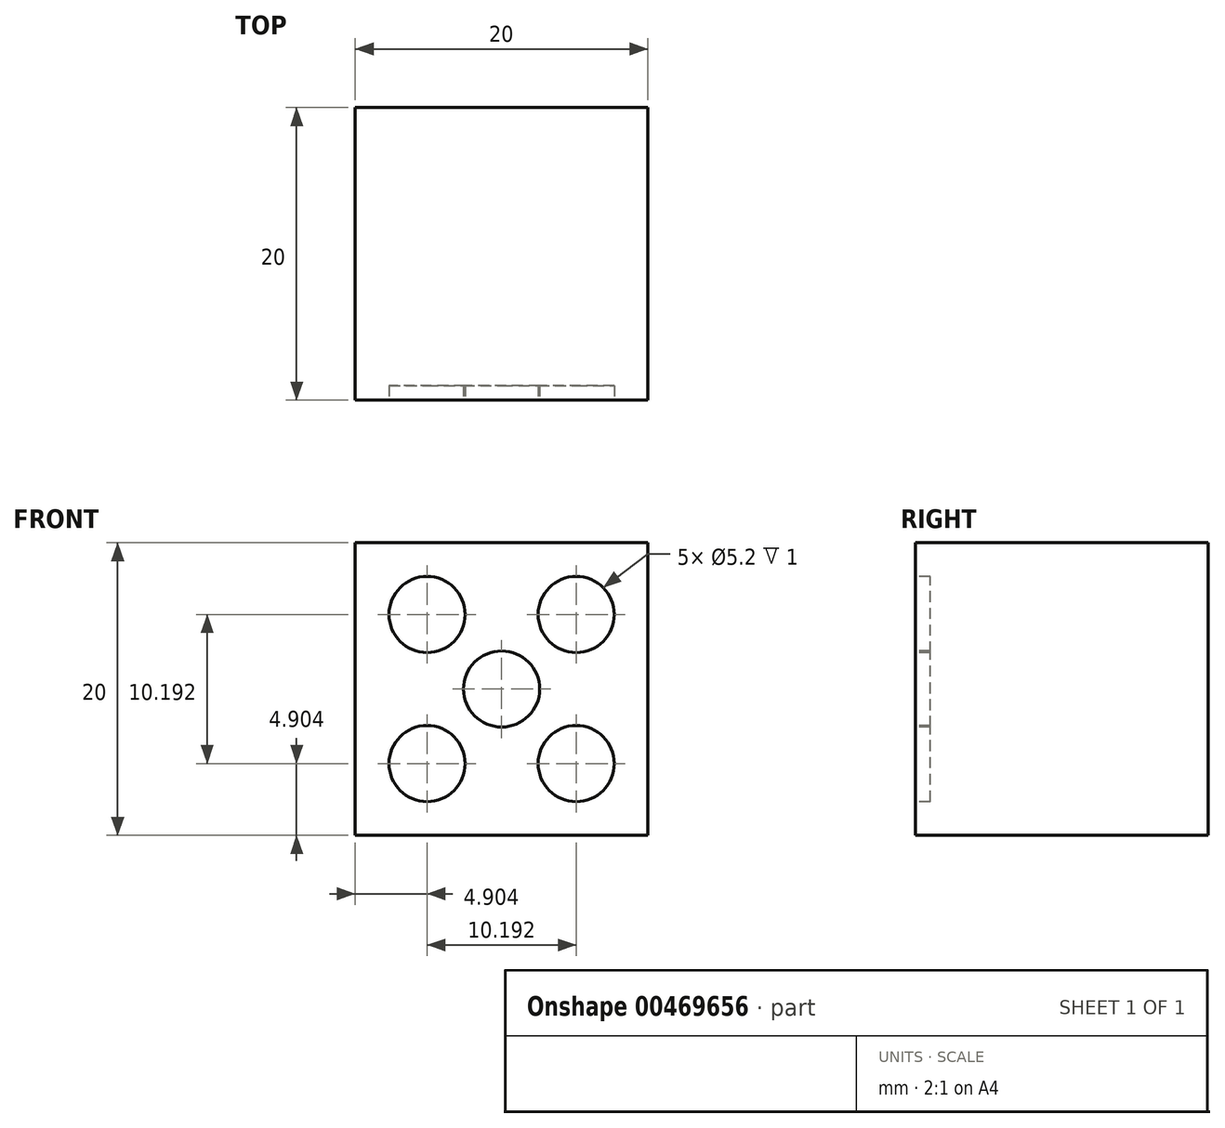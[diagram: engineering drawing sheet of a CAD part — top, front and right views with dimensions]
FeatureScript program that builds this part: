
annotation { "Feature Type Name" : "Feature", "Feature Type Description" : "" }
export const myFeature = defineFeature(function(context is Context, id is Id, definition is map)
    precondition{}
    {
        {
            var Q0;
            Q0=qCreatedBy(makeId("Front.planeOp"),FACE);
            var sketch = newSketch(context, id + "F0", { "sketchPlane" : qUnion([Q0])});
            skLineSegment(sketch, "E0.bottom", {"start": v(0, 0) * mm, "end": v(20, 0) * mm});
            skLineSegment(sketch, "E0.top", {"start": v(0, 20) * mm, "end": v(20, 20) * mm});
            skLineSegment(sketch, "E0.left", {"start": v(0, 0) * mm, "end": v(0, 20) * mm});
            skLineSegment(sketch, "E0.right", {"start": v(20, 0) * mm, "end": v(20, 20) * mm});
            skSolve(sketch);
        }
        {
            var Q0;
            Q0 = qSketchRegion(id + "F0", true);
            extrude(context, id + "F1", {"entities" : qUnion([Q0]), "depth" : 20 * mm});
        }
        {
            var Q0;
            Q0=makeQuery(id+"F1.opExtrude","CAP_FACE",FACE,{"disambiguationData":[OSD([sQuery(id+"F0.wireOp",EDGE,"E0.bottom"),sQuery(id+"F0.wireOp",EDGE,"E0.top"),sQuery(id+"F0.wireOp",EDGE,"E0.left"),sQuery(id+"F0.wireOp",EDGE,"E0.right")])],"isStart":false});
            var sketch = newSketch(context, id + "F2", { "sketchPlane" : qUnion([Q0])});
            skLineSegment(sketch, "E1", {"start": v(10, 20) * mm, "end": v(10, 0) * mm, "construction": true});
            skLineSegment(sketch, "E2", {"start": v(10, 0) * mm, "end": v(10, 20) * mm, "construction": true});
            skLineSegment(sketch, "E3", {"start": v(0, 10) * mm, "end": v(20, 10) * mm, "construction": true});
            skLineSegment(sketch, "E4", {"start": v(20, 10) * mm, "end": v(-0.94, 10) * mm, "construction": true});
            skLineSegment(sketch, "E5", {"start": v(-0.94, 10) * mm, "end": v(20, 10) * mm, "construction": true});
            skLineSegment(sketch, "E6", {"start": v(0, 20) * mm, "end": v(20, 0) * mm, "construction": true});
            skLineSegment(sketch, "E7", {"start": v(20, 0) * mm, "end": v(0, 20) * mm, "construction": true});
            skLineSegment(sketch, "E8", {"start": v(0, 0) * mm, "end": v(20, 20) * mm, "construction": true});
            skLineSegment(sketch, "E9", {"start": v(20, 20) * mm, "end": v(0, 0) * mm, "construction": true});
            skCircle(sketch, "E10", {"center": v(10, 10) * mm, "radius": 2.6 * mm});
            skCircle(sketch, "E11", {"center": v(4.9, 15.1) * mm, "radius": 2.6 * mm});
            skCircle(sketch, "E12.MirrorC", {"center": v(15.1, 15.1) * mm, "radius": 2.6 * mm});
            skLineSegment(sketch, "E13.MirrorCS", {"start": v(20.94, 10) * mm, "end": v(0, 10) * mm, "construction": true});
            skCircle(sketch, "E14.MirrorC", {"center": v(4.9, 4.9) * mm, "radius": 2.6 * mm});
            skCircle(sketch, "E15.MirrorC", {"center": v(15.1, 4.9) * mm, "radius": 2.6 * mm});
            skSolve(sketch);
        }
        {
            var Q0;
            Q0 = qSketchRegion(id + "F2", true);
            extrude(context, id + "F3", {"entities" : qUnion([Q0]), "operationType" : NewBodyOperationType.REMOVE, "oppositeDirection" : true, "depth" : 1 * mm});
        }
    });
